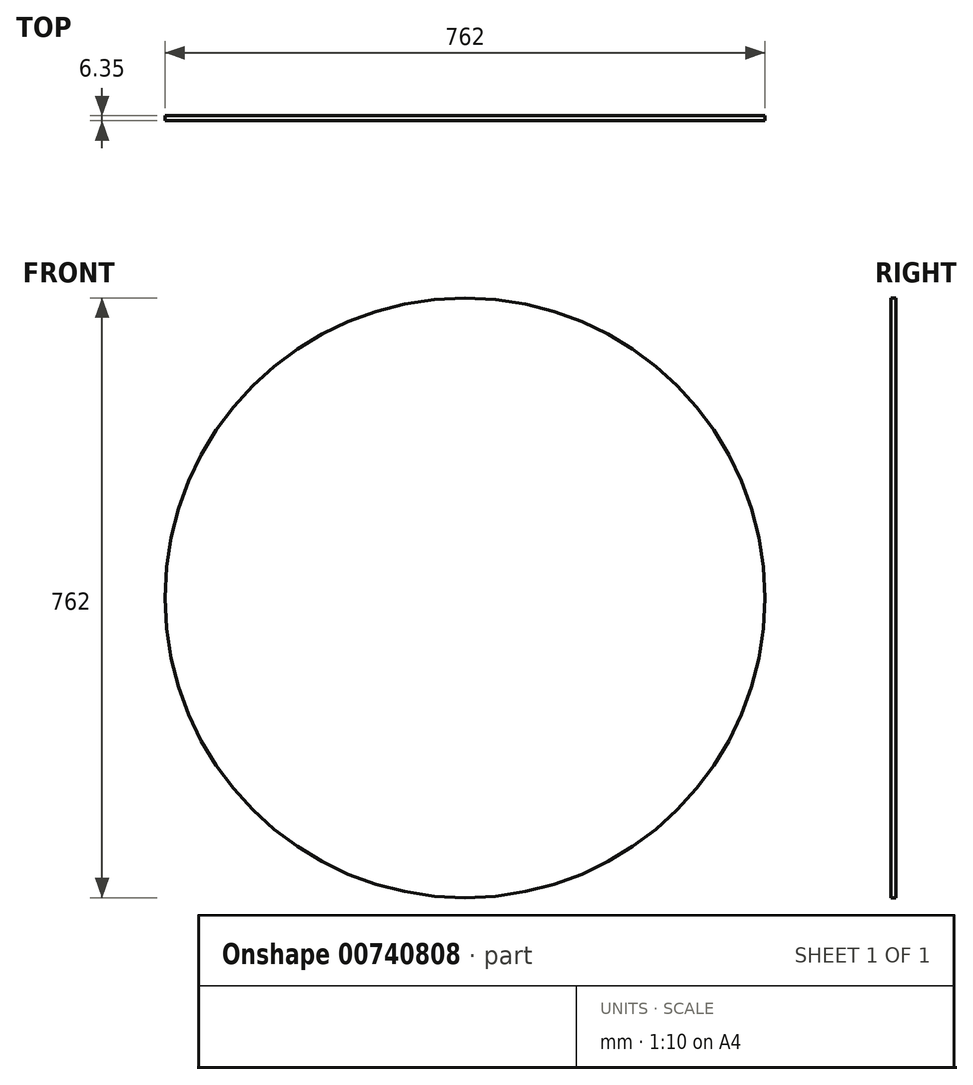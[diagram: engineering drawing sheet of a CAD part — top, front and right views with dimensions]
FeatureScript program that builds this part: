
annotation { "Feature Type Name" : "Feature", "Feature Type Description" : "" }
export const myFeature = defineFeature(function(context is Context, id is Id, definition is map)
    precondition{}
    {
        {
            var Q0;
            Q0=qCreatedBy(makeId("Front.planeOp"),FACE);
            var sketch = newSketch(context, id + "F0", { "sketchPlane" : qUnion([Q0])});
            skCircle(sketch, "E0", {"center": v(0, 0) * mm, "radius": 381 * mm});
            skSolve(sketch);
        }
        {
            var Q0;
            Q0 = qSketchRegion(id + "F0", true);
            extrude(context, id + "F1", {"entities" : qUnion([Q0]), "depth" : 6.35 * mm, "offsetDistance" : 25.4 * mm});
        }
    });
